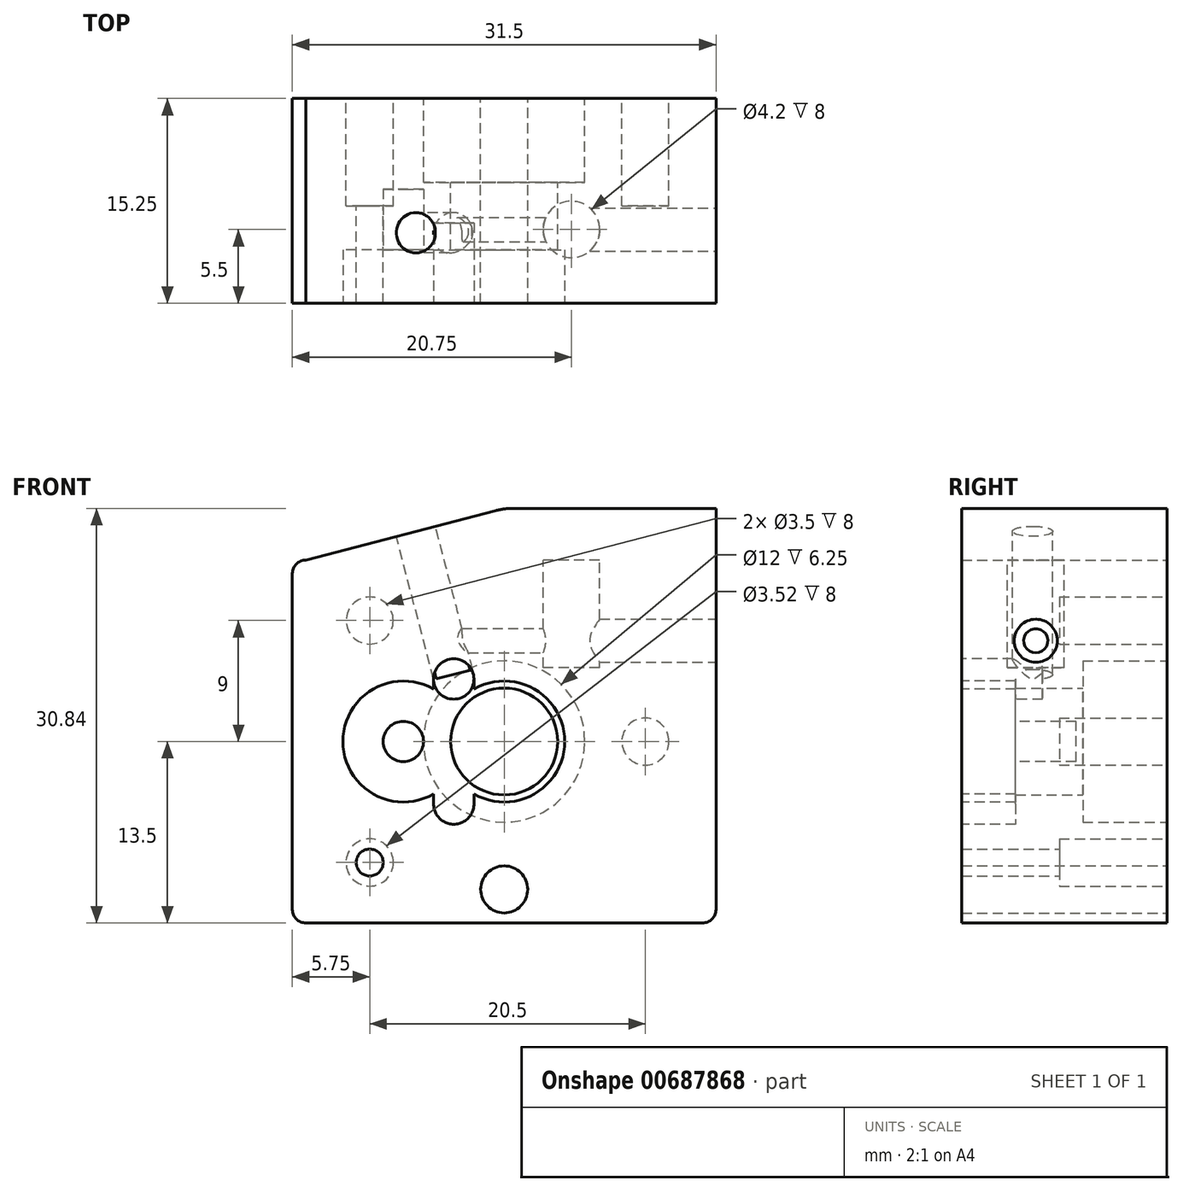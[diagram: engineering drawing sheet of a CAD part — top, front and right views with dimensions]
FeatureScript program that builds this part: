
annotation { "Feature Type Name" : "Feature", "Feature Type Description" : "" }
export const myFeature = defineFeature(function(context is Context, id is Id, definition is map)
    precondition{}
    {
        {
            var Q0;
            Q0=qCreatedBy(makeId("Front.planeOp"),FACE);
            var sketch = newSketch(context, id + "F0", { "sketchPlane" : qUnion([Q0])});
            skLineSegment(sketch, "E0.bottom", {"start": v(14.75, -13.5) * mm, "end": v(-14.75, -13.5) * mm});
            skLineSegment(sketch, "E0.top", {"start": v(14.75, 13.5) * mm, "end": v(-14.75, 13.5) * mm});
            skLineSegment(sketch, "E0.left", {"start": v(15.75, -12.5) * mm, "end": v(15.75, 12.5) * mm});
            skLineSegment(sketch, "E0.right", {"start": v(-15.75, -12.5) * mm, "end": v(-15.75, 12.5) * mm});
            skPoint(sketch, "E0.middle", {"position": v(0, 0) * mm});
            skCircle(sketch, "E1", {"center": v(0, 0) * mm, "radius": 3.98 * mm});
            skCircle(sketch, "E2", {"center": v(0, 0) * mm, "radius": 6 * mm});
            skPoint(sketch, "E3.visualSharp", {"position": v(-15.75, -13.5) * mm});
            skArc(sketch, "E3.filletArc", {"start": v(-15.75, -12.5) * mm, "mid": v(-15.46, -13.2) * mm, "end": v(-14.75, -13.5) * mm});
            skPoint(sketch, "E4.visualSharp", {"position": v(15.75, -13.5) * mm});
            skArc(sketch, "E4.filletArc", {"start": v(14.75, -13.5) * mm, "mid": v(15.46, -13.2) * mm, "end": v(15.75, -12.5) * mm});
            skPoint(sketch, "E5.visualSharp", {"position": v(-15.75, 13.5) * mm});
            skArc(sketch, "E5.filletArc", {"start": v(-14.75, 13.5) * mm, "mid": v(-15.46, 13.2) * mm, "end": v(-15.75, 12.5) * mm});
            skPoint(sketch, "E6.visualSharp", {"position": v(15.75, 13.5) * mm});
            skArc(sketch, "E6.filletArc", {"start": v(15.75, 12.5) * mm, "mid": v(15.46, 13.2) * mm, "end": v(14.75, 13.5) * mm});
            skSolve(sketch);
        }
        {
            var Q0;
            Q0=makeQuery(id+"F0.imprint","IMPRINT",FACE,{"disambiguationData":[TD([[makeQuery(id+"F0.imprint","IMPRINT",EDGE,{"derivedFrom":sQuery(id+"F0.wireOp",EDGE,"E0.bottom")}),-1.0]])]});
            var Q1;
            Q1=makeQuery(id+"F0.imprint","IMPRINT",FACE,{"disambiguationData":[TD([[makeQuery(id+"F0.imprint","IMPRINT",EDGE,{"derivedFrom":sQuery(id+"F0.wireOp",EDGE,"E1")}),-1.0]])]});
            extrude(context, id + "F1", {"entities" : qUnion([Q0, Q1]), "depth" : 15.25 * mm, "offsetDistance" : 25 * mm});
        }
        {
            var Q0;
            Q0=makeQuery(id+"F1.opExtrude","CAP_FACE",FACE,{"disambiguationData":[OSD([sQuery(id+"F0.wireOp",EDGE,"E0.bottom"),sQuery(id+"F0.wireOp",EDGE,"E0.top"),sQuery(id+"F0.wireOp",EDGE,"E0.left"),sQuery(id+"F0.wireOp",EDGE,"E0.right"),sQuery(id+"F0.wireOp",EDGE,"E1")])],"isStart":true});
            var sketch = newSketch(context, id + "F2", { "sketchPlane" : qUnion([Q0])});
            skCircle(sketch, "E7", {"center": v(0, 0) * mm, "radius": 6 * mm});
            skSolve(sketch);
        }
        {
            var Q0;
            Q0=makeQuery(id+"F2.imprint","IMPRINT",FACE,{"disambiguationData":[TD([[makeQuery(id+"F2.imprint","IMPRINT",EDGE,{"derivedFrom":sQuery(id+"F2.wireOp",EDGE,"E7")}),1.0]])]});
            var Q1;
            Q1=sQuery(id+"F2.wireOp",EDGE,"E7");
            extrude(context, id + "F3", {"entities" : qUnion([Q0]), "operationType" : NewBodyOperationType.REMOVE, "surfaceEntities" : qUnion([Q1]), "oppositeDirection" : true, "depth" : 6.25 * mm, "offsetDistance" : 25 * mm});
        }
        {
            var Q0;
            Q0=makeQuery(id+"F1.opExtrude","CAP_FACE",FACE,{"disambiguationData":[OSD([sQuery(id+"F0.wireOp",EDGE,"E0.bottom"),sQuery(id+"F0.wireOp",EDGE,"E0.top"),sQuery(id+"F0.wireOp",EDGE,"E0.left"),sQuery(id+"F0.wireOp",EDGE,"E0.right"),sQuery(id+"F0.wireOp",EDGE,"E1")])],"isStart":false});
            var sketch = newSketch(context, id + "F4", { "sketchPlane" : qUnion([Q0])});
            skArc(sketch, "E8", {"start": v(-2.25, -3.9) * mm, "mid": v(4.5, 0) * mm, "end": v(-2.25, 3.9) * mm});
            skArc(sketch, "E9", {"start": v(-5.25, 3.9) * mm, "mid": v(-12, 0) * mm, "end": v(-5.25, -3.9) * mm});
            skLineSegment(sketch, "E10", {"start": v(-3.75, 7.15) * mm, "end": v(-3.75, -9.18) * mm, "construction": true});
            skArc(sketch, "E11", {"start": v(-2.25, 4.65) * mm, "mid": v(-3.75, 6.15) * mm, "end": v(-5.25, 4.65) * mm});
            skArc(sketch, "E12", {"start": v(-5.25, -4.64) * mm, "mid": v(-3.75, -6.15) * mm, "end": v(-2.25, -4.64) * mm});
            skLineSegment(sketch, "E13", {"start": v(-14.34, 0) * mm, "end": v(6.48, 0) * mm, "construction": true});
            skLineSegment(sketch, "E14", {"start": v(-5.25, -4.66) * mm, "end": v(-5.25, -3.9) * mm});
            skLineSegment(sketch, "E15", {"start": v(-2.25, -4.66) * mm, "end": v(-2.25, -3.9) * mm});
            skLineSegment(sketch, "E16.trimOffspring", {"start": v(-5.25, 3.9) * mm, "end": v(-5.25, 4.65) * mm});
            skLineSegment(sketch, "E17.trimOffspring", {"start": v(-2.25, 3.9) * mm, "end": v(-2.25, 4.65) * mm});
            skSolve(sketch);
        }
        {
            var Q0;
            {var subQ1=sQuery(id+"F4.wireOp",EDGE,"E8");Q0=makeQuery(id+"F4.imprint","IMPRINT",FACE,{"disambiguationData":[TD([[makeQuery(id+"F4.imprint","IMPRINT",EDGE,{"derivedFrom":subQ1}),1.0]])]});}
            extrude(context, id + "F5", {"entities" : qUnion([Q0]), "operationType" : NewBodyOperationType.REMOVE, "oppositeDirection" : true, "depth" : 4 * mm, "offsetDistance" : 25 * mm});
        }
        {
            var Q0;
            Q0=makeQuery(id+"F5.boolean.opBoolean","COPY",FACE,{"derivedFrom":makeQuery(id+"F5.opExtrude","CAP_FACE",FACE,{"disambiguationData":[OSD([sQuery(id+"F0.wireOp",EDGE,"E1"),sQuery(id+"F4.wireOp",EDGE,"E8"),sQuery(id+"F4.wireOp",EDGE,"E9"),sQuery(id+"F4.wireOp",EDGE,"E11"),sQuery(id+"F4.wireOp",EDGE,"E12"),sQuery(id+"F4.wireOp",EDGE,"E14"),sQuery(id+"F4.wireOp",EDGE,"E15"),sQuery(id+"F4.wireOp",EDGE,"E16.trimOffspring"),sQuery(id+"F4.wireOp",EDGE,"E17.trimOffspring")])],"isStart":false})});
            var sketch = newSketch(context, id + "F6", { "sketchPlane" : qUnion([Q0])});
            skCircle(sketch, "E18", {"center": v(-7.5, 0) * mm, "radius": 1.5 * mm});
            skSolve(sketch);
        }
        {
            var Q0;
            Q0=makeQuery(id+"F6.imprint","IMPRINT",FACE,{"disambiguationData":[TD([[makeQuery(id+"F6.imprint","IMPRINT",EDGE,{"derivedFrom":sQuery(id+"F6.wireOp",EDGE,"E18")}),1.0]])]});
            var Q1;
            Q1=sQuery(id+"F6.wireOp",EDGE,"E18");
            extrude(context, id + "F7", {"entities" : qUnion([Q0]), "operationType" : NewBodyOperationType.REMOVE, "surfaceEntities" : qUnion([Q1]), "oppositeDirection" : true, "depth" : 4.5 * mm, "offsetDistance" : 25 * mm});
        }
        {
            var Q0;
            Q0=makeQuery(id+"F1.opExtrude","CAP_FACE",FACE,{"disambiguationData":[OSD([sQuery(id+"F0.wireOp",EDGE,"E0.bottom"),sQuery(id+"F0.wireOp",EDGE,"E0.top"),sQuery(id+"F0.wireOp",EDGE,"E0.left"),sQuery(id+"F0.wireOp",EDGE,"E0.right"),sQuery(id+"F0.wireOp",EDGE,"E1")])],"isStart":true});
            var sketch = newSketch(context, id + "F8", { "sketchPlane" : qUnion([Q0])});
            skCircle(sketch, "E19", {"center": v(0, -11) * mm, "radius": 1.75 * mm});
            skSolve(sketch);
        }
        {
            var Q0;
            Q0=makeQuery(id+"F8.imprint","IMPRINT",FACE,{"disambiguationData":[TD([[makeQuery(id+"F8.imprint","IMPRINT",EDGE,{"derivedFrom":sQuery(id+"F8.wireOp",EDGE,"E19")}),1.0]])]});
            var Q1;
            Q1=makeQuery(id+"F2eF08bL0DsZdCI_1.1.F8.imprint","IMPRINT",FACE,{"disambiguationData":[TD([[makeQuery(id+"F2eF08bL0DsZdCI_1.1.F8.imprint","IMPRINT",EDGE,{"derivedFrom":sQuery(id+"F2eF08bL0DsZdCI_1.1.F8.wireOp",EDGE,"E19")}),1.0]])]});
            var Q2;
            Q2=sQuery(id+"F8.wireOp",EDGE,"E19");
            var Q3;
            Q3=sQuery(id+"F2eF08bL0DsZdCI_1.1.F8.wireOp",EDGE,"E19");
            extrude(context, id + "F9", {"entities" : qUnion([Q0, Q1]), "operationType" : NewBodyOperationType.REMOVE, "surfaceEntities" : qUnion([Q2, Q3]), "endBound" : BoundingType.THROUGH_ALL, "oppositeDirection" : true, "depth" : 25 * mm, "offsetDistance" : 25 * mm});
        }
        {
            var Q0;
            Q0=makeQuery(id+"F1.opExtrude","CAP_FACE",FACE,{"disambiguationData":[OSD([sQuery(id+"F0.wireOp",EDGE,"E0.bottom"),sQuery(id+"F0.wireOp",EDGE,"E0.top"),sQuery(id+"F0.wireOp",EDGE,"E0.left"),sQuery(id+"F0.wireOp",EDGE,"E0.right"),sQuery(id+"F0.wireOp",EDGE,"E1")])],"isStart":true});
            var sketch = newSketch(context, id + "F10", { "sketchPlane" : qUnion([Q0])});
            skCircle(sketch, "E20", {"center": v(-10.5, 0) * mm, "radius": 1 * mm});
            skCircle(sketch, "E21", {"center": v(10, -9) * mm, "radius": 1 * mm});
            skSolve(sketch);
        }
        {
            var Q0;
            Q0=makeQuery(id+"F10.imprint","IMPRINT",FACE,{"disambiguationData":[TD([[makeQuery(id+"F10.imprint","IMPRINT",EDGE,{"derivedFrom":sQuery(id+"F10.wireOp",EDGE,"E21")}),1.0]])]});
            var Q1;
            Q1=makeQuery(id+"FlKXs7Ng7FWXYm4_1.1.F10.imprint","IMPRINT",FACE,{"disambiguationData":[TD([[makeQuery(id+"FlKXs7Ng7FWXYm4_1.1.F10.imprint","IMPRINT",EDGE,{"derivedFrom":sQuery(id+"FlKXs7Ng7FWXYm4_1.1.F10.wireOp",EDGE,"E20")}),1.0]])]});
            var Q2;
            Q2=makeQuery(id+"FlKXs7Ng7FWXYm4_1.1.F10.imprint","IMPRINT",FACE,{"disambiguationData":[TD([[makeQuery(id+"FlKXs7Ng7FWXYm4_1.1.F10.imprint","IMPRINT",EDGE,{"derivedFrom":sQuery(id+"FlKXs7Ng7FWXYm4_1.1.F10.wireOp",EDGE,"E21")}),1.0]])]});
            var Q3;
            Q3=sQuery(id+"F10.wireOp",EDGE,"E21");
            var Q4;
            Q4=sQuery(id+"FlKXs7Ng7FWXYm4_1.1.F10.wireOp",EDGE,"E20");
            var Q5;
            Q5=sQuery(id+"FlKXs7Ng7FWXYm4_1.1.F10.wireOp",EDGE,"E21");
            extrude(context, id + "F11", {"entities" : qUnion([Q0, Q1, Q2]), "operationType" : NewBodyOperationType.REMOVE, "surfaceEntities" : qUnion([Q3, Q4, Q5]), "endBound" : BoundingType.THROUGH_ALL, "oppositeDirection" : true, "depth" : 25 * mm, "offsetDistance" : 25 * mm});
        }
        {
            var Q0;
            Q0=makeQuery(id+"F1.opExtrude","CAP_FACE",FACE,{"disambiguationData":[OSD([sQuery(id+"F0.wireOp",EDGE,"E0.bottom"),sQuery(id+"F0.wireOp",EDGE,"E0.top"),sQuery(id+"F0.wireOp",EDGE,"E0.left"),sQuery(id+"F0.wireOp",EDGE,"E0.right"),sQuery(id+"F0.wireOp",EDGE,"E1")])],"isStart":true});
            var sketch = newSketch(context, id + "F12", { "sketchPlane" : qUnion([Q0])});
            skCircle(sketch, "E22", {"center": v(10, -9) * mm, "radius": 1.76 * mm});
            skCircle(sketch, "E23", {"center": v(10, 9) * mm, "radius": 1.75 * mm});
            skCircle(sketch, "E24", {"center": v(-10.5, 0) * mm, "radius": 1.75 * mm});
            skSolve(sketch);
        }
        {
            var Q0;
            Q0=makeQuery(id+"F12.imprint","IMPRINT",FACE,{"disambiguationData":[TD([[makeQuery(id+"F12.imprint","IMPRINT",EDGE,{"derivedFrom":sQuery(id+"F12.wireOp",EDGE,"E22")}),1.0]])]});
            var Q1;
            Q1=makeQuery(id+"F12.imprint","IMPRINT",FACE,{"disambiguationData":[TD([[makeQuery(id+"F12.imprint","IMPRINT",EDGE,{"derivedFrom":sQuery(id+"F12.wireOp",EDGE,"E24")}),1.0]])]});
            var Q2;
            Q2=makeQuery(id+"F12.imprint","IMPRINT",FACE,{"disambiguationData":[TD([[makeQuery(id+"F12.imprint","IMPRINT",EDGE,{"derivedFrom":sQuery(id+"F12.wireOp",EDGE,"E23")}),1.0]])]});
            extrude(context, id + "F13", {"entities" : qUnion([Q0, Q1, Q2]), "operationType" : NewBodyOperationType.REMOVE, "oppositeDirection" : true, "depth" : 8 * mm, "offsetDistance" : 25 * mm});
        }
        {
            var Q0;
            Q0=makeQuery(id+"F1.opExtrude","SWEPT_FACE",FACE,{"disambiguationData":[OSD([sQuery(id+"F0.wireOp",EDGE,"E0.top")])]});
            var sketch = newSketch(context, id + "F14", { "sketchPlane" : qUnion([Q0])});
            skCircle(sketch, "E25", {"center": v(5, -9.75) * mm, "radius": 2.1 * mm});
            skSolve(sketch);
        }
        {
            var Q0;
            Q0=makeQuery(id+"F14.imprint","IMPRINT",FACE,{"disambiguationData":[TD([[makeQuery(id+"F14.imprint","IMPRINT",EDGE,{"derivedFrom":sQuery(id+"F14.wireOp",EDGE,"E25")}),1.0]])]});
            extrude(context, id + "F15", {"entities" : qUnion([Q0]), "operationType" : NewBodyOperationType.REMOVE, "oppositeDirection" : true, "depth" : 8 * mm, "offsetDistance" : 25 * mm});
        }
        {
            var Q0;
            Q0=makeQuery(id+"F5.boolean.opBoolean","COPY",FACE,{"derivedFrom":makeQuery(id+"F5.opExtrude","CAP_FACE",FACE,{"disambiguationData":[OSD([sQuery(id+"F0.wireOp",EDGE,"E1"),sQuery(id+"F4.wireOp",EDGE,"E8"),sQuery(id+"F4.wireOp",EDGE,"E9"),sQuery(id+"F4.wireOp",EDGE,"E11"),sQuery(id+"F4.wireOp",EDGE,"E12"),sQuery(id+"F4.wireOp",EDGE,"E14"),sQuery(id+"F4.wireOp",EDGE,"E15"),sQuery(id+"F4.wireOp",EDGE,"E16.trimOffspring"),sQuery(id+"F4.wireOp",EDGE,"E17.trimOffspring")])],"isStart":false})});
            var sketch = newSketch(context, id + "F16", { "sketchPlane" : qUnion([Q0])});
            skCircle(sketch, "E26", {"center": v(-3.75, 4.65) * mm, "radius": 1.5 * mm});
            skSolve(sketch);
        }
        {
            var Q0;
            {var subQ1=sQuery(id+"F4.wireOp",EDGE,"E17.trimOffspring");var subQ5=sQuery(id+"F16.wireOp",EDGE,"E26");var subQ8=makeQuery(id+"F16.imprint","INTERSECT",VERTEX,{"derivedFrom":[makeQuery(id+"F5.boolean.opBoolean","COPY",EDGE,{"derivedFrom":makeQuery(id+"F5.opExtrude","CAP_EDGE",EDGE,{"disambiguationData":[OSD([subQ1])],"isStart":false})}),subQ5]});Q0=makeQuery(id+"F16.imprint","IMPRINT",FACE,{"disambiguationData":[TD([[makeQuery(id+"F16.imprint","IMPRINT",EDGE,{"disambiguationData":[TD([[subQ8,1.0]])],"derivedFrom":subQ5}),1.0]])]});}
            extrude(context, id + "F17", {"entities" : qUnion([Q0]), "operationType" : NewBodyOperationType.REMOVE, "oppositeDirection" : true, "depth" : 2 * mm, "offsetDistance" : 25 * mm});
        }
        {
            var Q0;
            Q0=makeQuery(id+"F1.opExtrude","SWEPT_FACE",FACE,{"disambiguationData":[OSD([sQuery(id+"F0.wireOp",EDGE,"E0.left")])]});
            var sketch = newSketch(context, id + "F18", { "sketchPlane" : qUnion([Q0])});
            skCircle(sketch, "E27", {"center": v(-9.75, 7.5) * mm, "radius": 1.6 * mm});
            skSolve(sketch);
        }
        {
            var Q0;
            Q0=makeQuery(id+"F18.imprint","IMPRINT",FACE,{"disambiguationData":[TD([[makeQuery(id+"F18.imprint","IMPRINT",EDGE,{"derivedFrom":sQuery(id+"F18.wireOp",EDGE,"E27")}),1.0]])]});
            extrude(context, id + "F19", {"entities" : qUnion([Q0]), "operationType" : NewBodyOperationType.REMOVE, "oppositeDirection" : true, "depth" : 12 * mm, "offsetDistance" : 25 * mm});
        }
        {
            var Q0;
            Q0=makeQuery(id+"F1.opExtrude","SWEPT_FACE",FACE,{"disambiguationData":[OSD([sQuery(id+"F0.wireOp",EDGE,"E0.left")])]});
            var sketch = newSketch(context, id + "F20", { "sketchPlane" : qUnion([Q0])});
            skCircle(sketch, "E28", {"center": v(-9.75, 7.5) * mm, "radius": 0.9 * mm});
            skSolve(sketch);
        }
        {
            var Q0;
            Q0 = qSketchRegion(id + "F20", true);
            extrude(context, id + "F21", {"entities" : qUnion([Q0]), "operationType" : NewBodyOperationType.REMOVE, "oppositeDirection" : true, "depth" : 20 * mm, "offsetDistance" : 25 * mm});
        }
        {
            var Q0;
            Q0=makeQuery(id+"F1.opExtrude","CAP_FACE",FACE,{"disambiguationData":[OSD([sQuery(id+"F0.wireOp",EDGE,"E0.bottom"),sQuery(id+"F0.wireOp",EDGE,"E0.top"),sQuery(id+"F0.wireOp",EDGE,"E0.left"),sQuery(id+"F0.wireOp",EDGE,"E0.right"),sQuery(id+"F0.wireOp",EDGE,"E1"),sQuery(id+"F0.wireOp",EDGE,"E3.filletArc"),sQuery(id+"F0.wireOp",EDGE,"E4.filletArc"),sQuery(id+"F0.wireOp",EDGE,"E5.filletArc"),sQuery(id+"F0.wireOp",EDGE,"E6.filletArc")])],"isStart":false});
            var sketch = newSketch(context, id + "F22", { "sketchPlane" : qUnion([Q0])});
            skLineSegment(sketch, "E29", {"start": v(-3.76, 4.76) * mm, "end": v(-6.97, 17.08) * mm, "construction": true});
            skLineSegment(sketch, "E30", {"start": v(-14.75, 13.5) * mm, "end": v(-0.62, 17.18) * mm});
            skLineSegment(sketch, "E31", {"start": v(0.64, 17.34) * mm, "end": v(15.75, 17.34) * mm});
            skLineSegment(sketch, "E32", {"start": v(15.75, 17.34) * mm, "end": v(15.75, 12.5) * mm});
            skPoint(sketch, "E33.visualSharp", {"position": v(0, 17.34) * mm});
            skArc(sketch, "E33.filletArc", {"start": v(0.64, 17.34) * mm, "mid": v(0, 17.3) * mm, "end": v(-0.62, 17.18) * mm});
            skSolve(sketch);
        }
        {
            var Q0;
            Q0=makeQuery(id+"F22.imprint","IMPRINT",FACE,{"disambiguationData":[TD([[makeQuery(id+"F22.imprint","IMPRINT",EDGE,{"derivedFrom":sQuery(id+"F22.wireOp",EDGE,"E30")}),-1.0]])]});
            var Q1;
            Q1=makeQuery(id+"F1.opExtrude","CAP_FACE",FACE,{"disambiguationData":[OSD([sQuery(id+"F0.wireOp",EDGE,"E0.bottom"),sQuery(id+"F0.wireOp",EDGE,"E0.top"),sQuery(id+"F0.wireOp",EDGE,"E0.left"),sQuery(id+"F0.wireOp",EDGE,"E0.right"),sQuery(id+"F0.wireOp",EDGE,"E1"),sQuery(id+"F0.wireOp",EDGE,"E3.filletArc"),sQuery(id+"F0.wireOp",EDGE,"E4.filletArc"),sQuery(id+"F0.wireOp",EDGE,"E5.filletArc"),sQuery(id+"F0.wireOp",EDGE,"E6.filletArc")])],"isStart":true});
            extrude(context, id + "F23", {"entities" : qUnion([Q0]), "operationType" : NewBodyOperationType.ADD, "endBound" : BoundingType.UP_TO_SURFACE, "oppositeDirection" : true, "depth" : 25 * mm, "endBoundEntityFace" : qUnion([Q1]), "offsetDistance" : 25 * mm});
        }
        {
            var Q0;
            Q0=makeQuery(id+"F23.opExtrude","SWEPT_FACE",FACE,{"disambiguationData":[OSD([sQuery(id+"F22.wireOp",EDGE,"E30")])]});
            var sketch = newSketch(context, id + "F24", { "sketchPlane" : qUnion([Q0])});
            skPoint(sketch, "E34.centerSnap0", {"position": v(-3.57, -15.25) * mm});
            skCircle(sketch, "E35", {"center": v(-2.41, -10) * mm, "radius": 1.5 * mm});
            skSolve(sketch);
        }
        {
            var Q0;
            Q0 = qSketchRegion(id + "F24", true);
            extrude(context, id + "F25", {"entities" : qUnion([Q0]), "operationType" : NewBodyOperationType.REMOVE, "oppositeDirection" : true, "depth" : 11 * mm, "offsetDistance" : 25 * mm});
        }
    });
